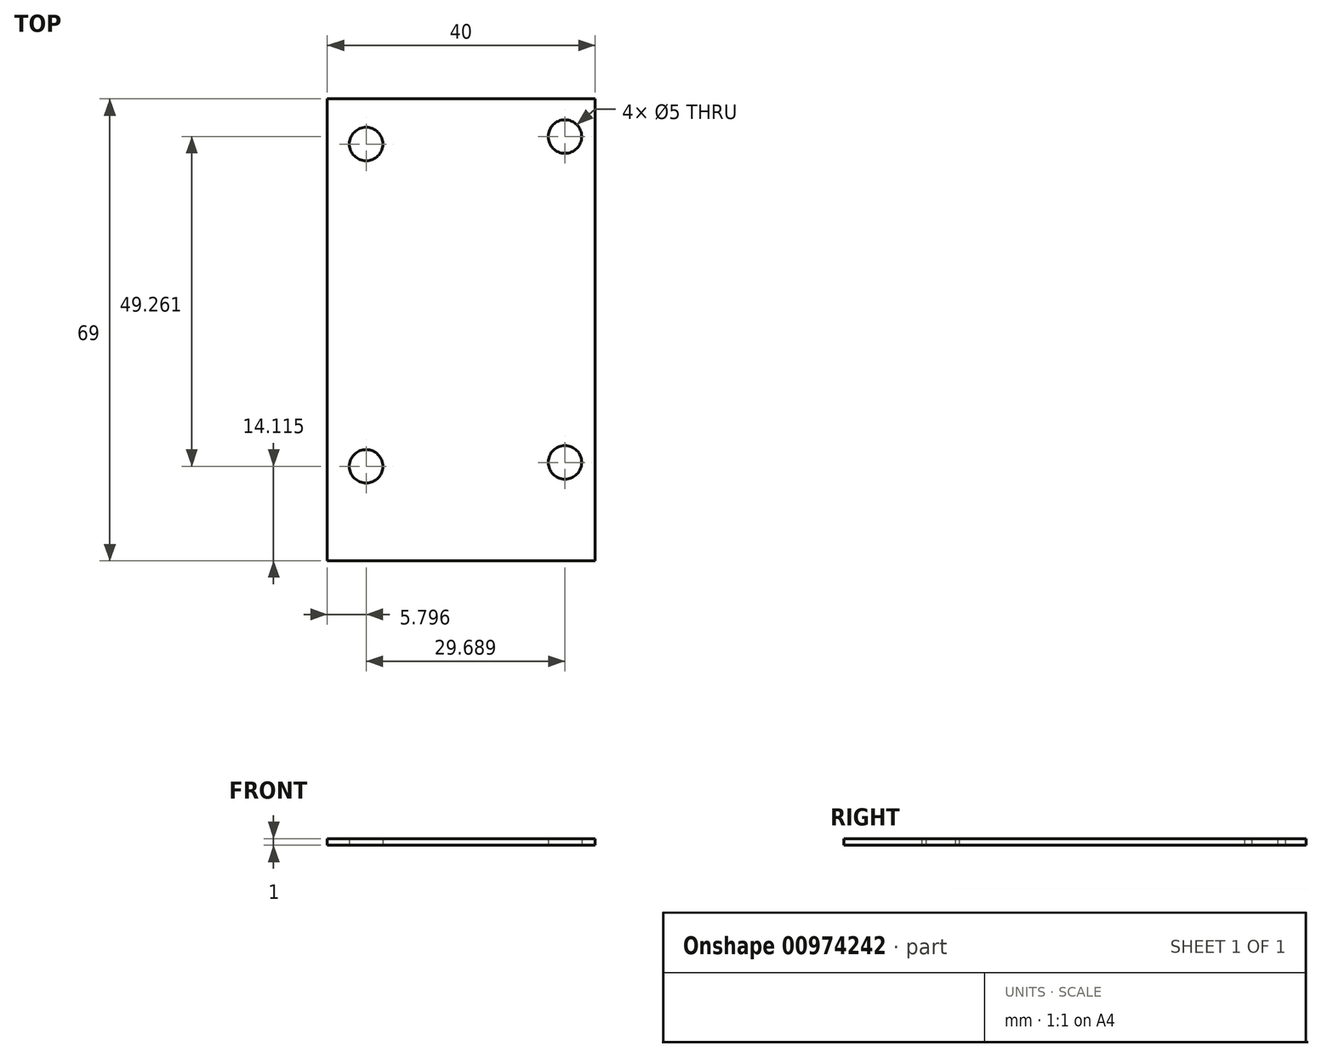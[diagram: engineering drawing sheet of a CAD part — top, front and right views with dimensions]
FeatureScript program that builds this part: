
annotation { "Feature Type Name" : "Feature", "Feature Type Description" : "" }
export const myFeature = defineFeature(function(context is Context, id is Id, definition is map)
    precondition{}
    {
        {
            var Q0;
            Q0=qCreatedBy(makeId("Top.planeOp"),FACE);
            var sketch = newSketch(context, id + "F0", { "sketchPlane" : qUnion([Q0])});
            skLineSegment(sketch, "E0.bottom", {"start": v(-20, 34.5) * mm, "end": v(20, 34.5) * mm});
            skLineSegment(sketch, "E0.top", {"start": v(-20, -34.5) * mm, "end": v(20, -34.5) * mm});
            skLineSegment(sketch, "E0.left", {"start": v(-20, 34.5) * mm, "end": v(-20, -34.5) * mm});
            skLineSegment(sketch, "E0.right", {"start": v(20, 34.5) * mm, "end": v(20, -34.5) * mm});
            skCircle(sketch, "E1", {"center": v(-14.2, 27.76) * mm, "radius": 2.5 * mm});
            skCircle(sketch, "E2", {"center": v(-14.2, -20.39) * mm, "radius": 2.5 * mm});
            skCircle(sketch, "E3", {"center": v(15.48, 28.88) * mm, "radius": 2.5 * mm});
            skCircle(sketch, "E4", {"center": v(15.48, -19.8) * mm, "radius": 2.5 * mm});
            skSolve(sketch);
        }
        {
            var Q0;
            Q0 = qSketchRegion(id + "F0", true);
            extrude(context, id + "F1", {"entities" : qUnion([Q0]), "depth" : 1 * mm, "offsetDistance" : 25 * mm});
        }
    });
